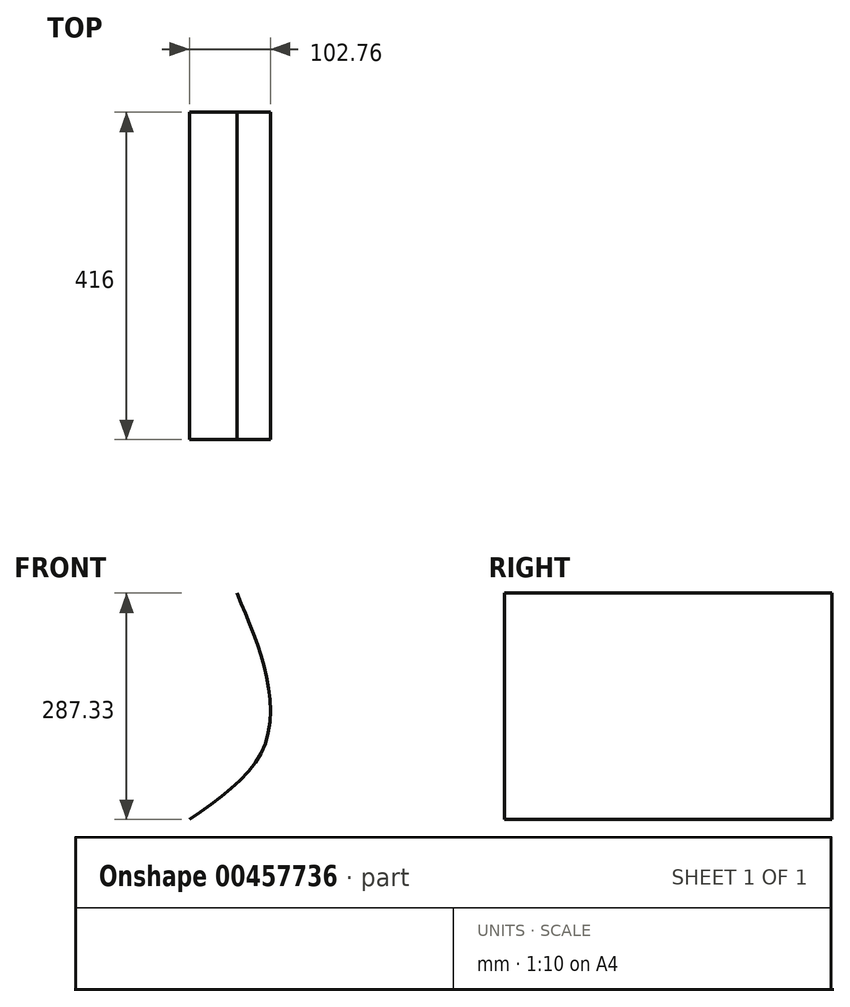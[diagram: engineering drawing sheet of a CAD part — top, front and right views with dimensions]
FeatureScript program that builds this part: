
annotation { "Feature Type Name" : "Feature", "Feature Type Description" : "" }
export const myFeature = defineFeature(function(context is Context, id is Id, definition is map)
    precondition{}
    {
        {
            var Q0;
            Q0=qCreatedBy(makeId("Front.planeOp"),FACE);
            var sketch = newSketch(context, id + "F0", { "sketchPlane" : qUnion([Q0])});
            skFitSpline(sketch, "E0", {"points": [v(-65.67, 150.24) * mm, v(-29.57, 51.06) * mm, v(-33.74, -50.83) * mm, v(-125.84, -137.09) * mm], "startDerivative": vector(128.7, -296.6) * mm, "endDerivative": vector(-319.36, -220.4) * mm});
            skSolve(sketch);
        }
        {
            var Q0;
            Q0=sQuery(id+"F0.wireOp",EDGE,"E0");
            extrude(context, id + "F1", {"bodyType" : ToolBodyType.SURFACE, "surfaceEntities" : qUnion([Q0]), "endBound" : BoundingType.SYMMETRIC, "depth" : 416 * mm});
        }
    });
